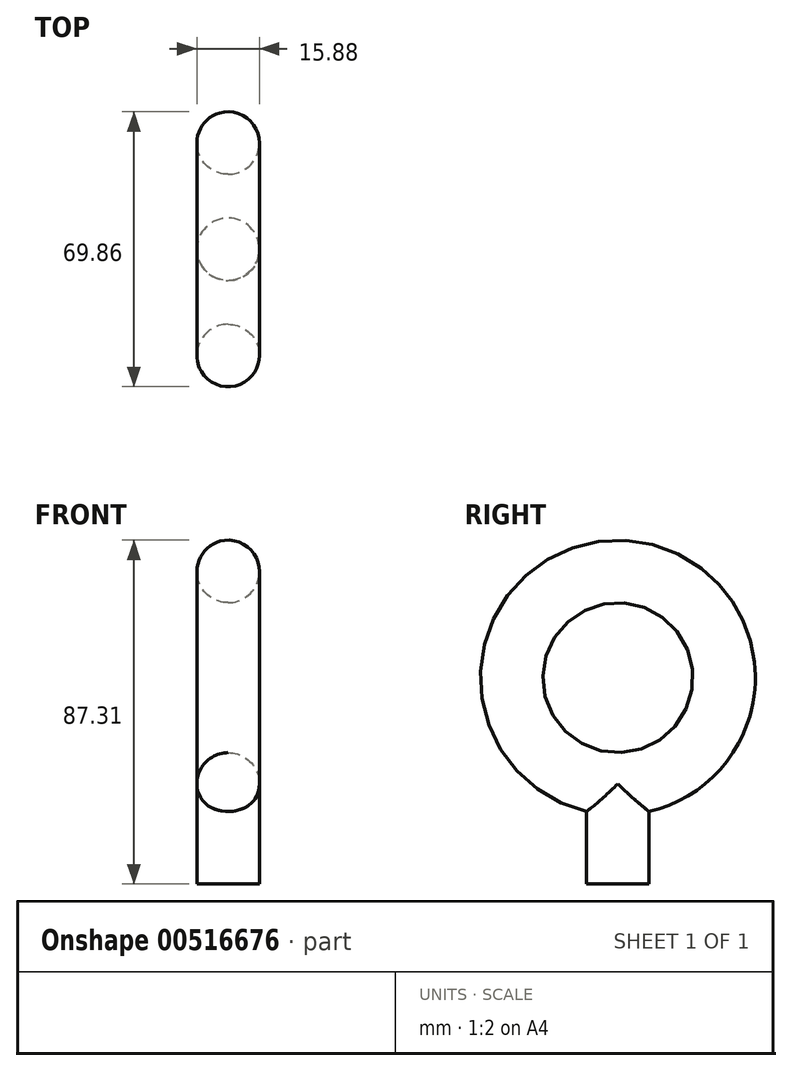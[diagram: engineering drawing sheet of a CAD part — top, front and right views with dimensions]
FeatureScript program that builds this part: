
annotation { "Feature Type Name" : "Feature", "Feature Type Description" : "" }
export const myFeature = defineFeature(function(context is Context, id is Id, definition is map)
    precondition{}
    {
        {
            var Q0;
            Q0=qCreatedBy(makeId("Front.planeOp"),FACE);
            var sketch = newSketch(context, id + "F0", { "sketchPlane" : qUnion([Q0])});
            skPoint(sketch, "E0.first.point", {"position": v(0, 0) * mm});
            skLineSegment(sketch, "E1", {"start": v(-15.39, 26.99) * mm, "end": v(15.5, 26.99) * mm, "construction": true});
            skCircle(sketch, "E2", {"center": v(0, 0) * mm, "radius": 7.94 * mm});
            skSolve(sketch);
        }
        {
            var Q0;
            Q0=makeQuery(id+"F0.imprint","IMPRINT",FACE,{"disambiguationData":[TD([[makeQuery(id+"F0.imprint","IMPRINT",EDGE,{"derivedFrom":sQuery(id+"F0.wireOp",EDGE,"E2")}),1.0]])]});
            var Q1;
            Q1=sQuery(id+"F0.wireOp",EDGE,"E1");
            revolve(context, id + "F1", {"entities" : qUnion([Q0]), "axis" : qUnion([Q1]), "revolveType" : RevolveType.FULL});
        }
        {
            var Q0;
            Q0=qCreatedBy(makeId("Top.planeOp"),FACE);
            var sketch = newSketch(context, id + "F2", { "sketchPlane" : qUnion([Q0])});
            skCircle(sketch, "E3", {"center": v(0, 0) * mm, "radius": 7.94 * mm});
            skSolve(sketch);
        }
        {
            var Q0;
            Q0=makeQuery(id+"F2.imprint","IMPRINT",FACE,{"disambiguationData":[TD([[makeQuery(id+"F2.imprint","IMPRINT",EDGE,{"derivedFrom":sQuery(id+"F2.wireOp",EDGE,"E3")}),1.0]])]});
            extrude(context, id + "F3", {"entities" : qUnion([Q0]), "operationType" : NewBodyOperationType.ADD, "oppositeDirection" : true, "depth" : 25.4 * mm, "offsetDistance" : 25.4 * mm});
        }
    });
